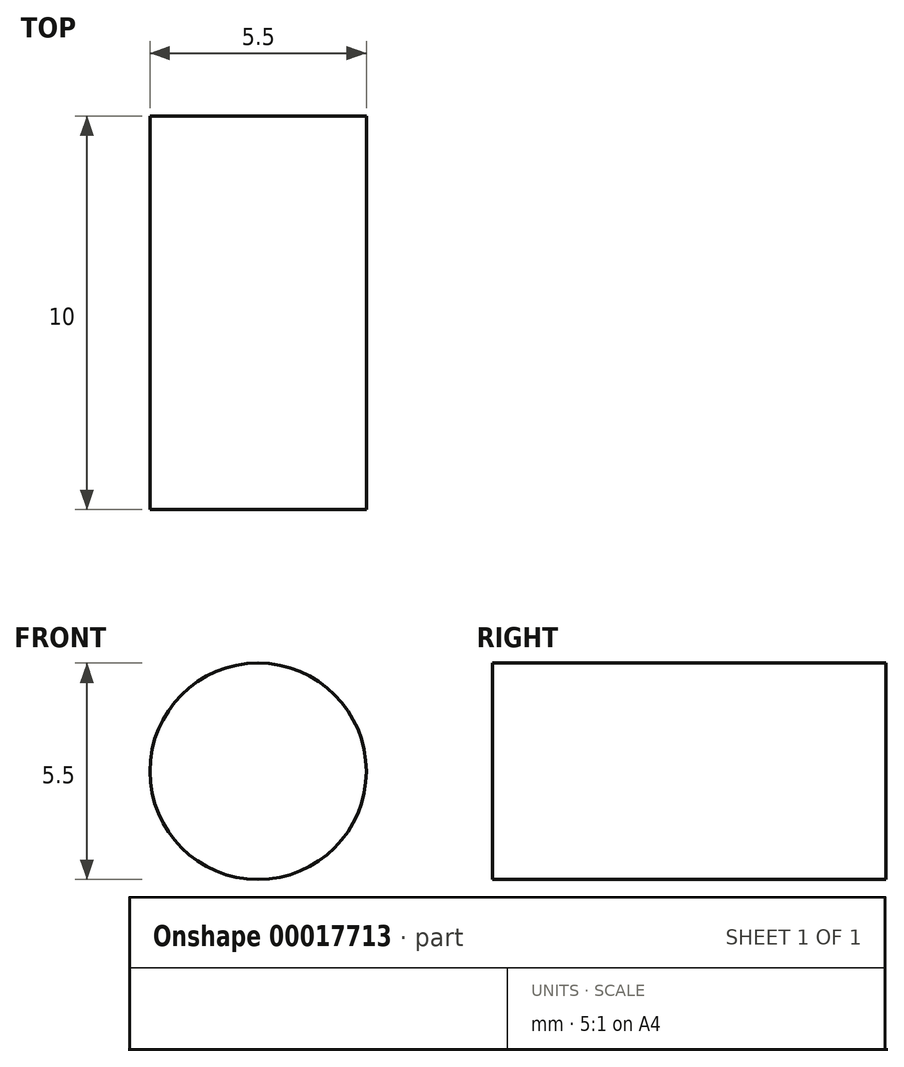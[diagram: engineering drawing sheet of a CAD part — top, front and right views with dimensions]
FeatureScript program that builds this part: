
annotation { "Feature Type Name" : "Feature", "Feature Type Description" : "" }
export const myFeature = defineFeature(function(context is Context, id is Id, definition is map)
    precondition{}
    {
        {
            var Q0;
            Q0=qCreatedBy(makeId("Front.planeOp"),FACE);
            var sketch = newSketch(context, id + "F0", { "sketchPlane" : qUnion([Q0])});
            skCircle(sketch, "E0", {"center": v(0, 0) * mm, "radius": 2.75 * mm});
            skSolve(sketch);
        }
        {
            var Q0;
            Q0 = qSketchRegion(id + "F0", true);
            extrude(context, id + "F1", {"entities" : qUnion([Q0]), "depth" : 10 * mm});
        }
    });
